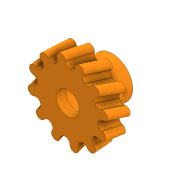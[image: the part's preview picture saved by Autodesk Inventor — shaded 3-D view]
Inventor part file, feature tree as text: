
AUTODESK INVENTOR PART (.ipt)
format: ipt  version: 2020 (Build 240168000, 168)  size: 476,160 bytes
history: native  units: in
note: dims shown in document units (in); Inventor stores cm internally (conversion verified against a paired STEP export)
features: sketch x7, extrude x5, plane x1, sweep x1, fillet x1, chamfer x1, other x1, projected_geometry x1
ambient origin geometry x8: Origin, YZ Plane, XZ Plane, XY Plane, X Axis, Y Axis, Z Axis, Center Point
bodies: Solid1 (feature_tree)
feature tree (18):
  extrude  "Extrusion1"  Depth=0.315in
  plane  "Work Plane1"
  sweep  "Sweep1"
  extrude  "Extrusion3"  Depth=0.0866in
  extrude  "Extrusion4"  Depth=0.0787in
  extrude  "Extrusion5"  Depth=4.7244in TaperAngle=360.0deg
  extrude  "Extrusion6"  TaperAngle=0.0deg  [1 undecoded]
  fillet  "Fillet1"  Radius=1.0in
  chamfer  "Chamfer1"  Distance=0.2008in
  sketch  "Sketch1"  dims[d0=0.4724in d1=0.315in]
  sketch  "Sketch3"  dims[d2=2.5197in d3=0.0in d7=-0.1969in]
  sketch  "3D Sketch1"
  other  "Helical Curve1"
  sketch  "Sketch4"  dims[d8=0.7087in d9=0.0866in]
  projected_geometry  "Projected Loop1"
  sketch  "Sketch5"  dims[d10=0.0787in d11=0.0787in]
  sketch  "Sketch6"  dims[d12=0.0787in d13=4.7244in d15=360.0deg]
  sketch  "Sketch7"  dims[d17=0.1969in d18=0.0118in d19=0.535in d20=0.0in d21=0.0in d22=0.0in d23=1.0in d24=0.0in d25=0.2008in d26=1.0in d27=0.0in d28=0.0787in d29=0.1969in d30=0.0in d31=0.0748in d32=0.1969in d33=0.0in d34=0.0118in d35=0.315in d36=0.125in d37=0.0137in]
note: 1 required parameter value undecoded (feature->parameter linkage not recoverable at this tier; creation-order binding heuristic only, values carry confidence <= 0.55)
